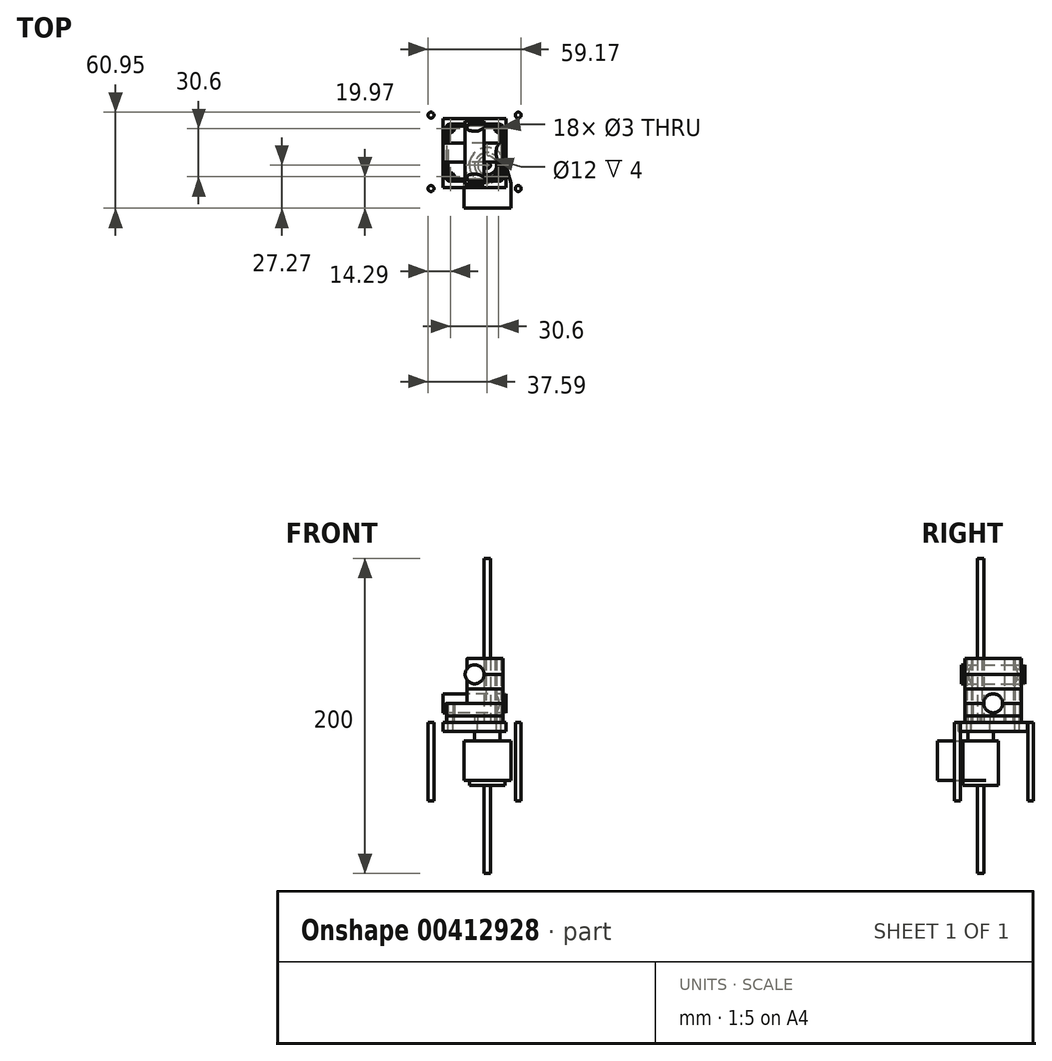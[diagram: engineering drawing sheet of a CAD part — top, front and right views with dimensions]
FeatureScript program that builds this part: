
annotation { "Feature Type Name" : "Feature", "Feature Type Description" : "" }
export const myFeature = defineFeature(function(context is Context, id is Id, definition is map)
    precondition{}
    {
        {
            var Q0;
            Q0=qCreatedBy(makeId("Top.planeOp"),FACE);
            cPlane(context, id + "F0", {"entities" : qUnion([Q0]), "cplaneType" : CPlaneType.OFFSET, "offset" : 3 * mm, "width" : 150 * mm, "height" : 150 * mm});
        }
        {
            var Q0;
            Q0=qCreatedBy(makeId("Top.planeOp"),FACE);
            cPlane(context, id + "F1", {"entities" : qUnion([Q0]), "cplaneType" : CPlaneType.OFFSET, "offset" : 1 * mm, "oppositeDirection" : true, "width" : 150 * mm, "height" : 150 * mm});
        }
        {
            var Q0;
            Q0=qCreatedBy(makeId("Right.planeOp"),FACE);
            var sketch = newSketch(context, id + "F2", { "sketchPlane" : qUnion([Q0])});
            skLineSegment(sketch, "E0", {"start": v(0, 0) * mm, "end": v(0, 11) * mm, "construction": true});
            skCircle(sketch, "E1", {"center": v(0, 11) * mm, "radius": 6 * mm});
            skSolve(sketch);
        }
        {
            var Q0;
            Q0=qCreatedBy(makeId("Front.planeOp"),FACE);
            var sketch = newSketch(context, id + "F3", { "sketchPlane" : qUnion([Q0])});
            skLineSegment(sketch, "E2", {"start": v(0, 0) * mm, "end": v(0, 29.4) * mm, "construction": true});
            skCircle(sketch, "E3", {"center": v(0, 29.4) * mm, "radius": 6 * mm});
            skSolve(sketch);
        }
        {
            var Q0;
            Q0=makeQuery(id+"F2.imprint","IMPRINT",FACE,{"disambiguationData":[TD([[makeQuery(id+"F2.imprint","IMPRINT",EDGE,{"derivedFrom":sQuery(id+"F2.wireOp",EDGE,"E1")}),1.0]])]});
            extrude(context, id + "F4", {"entities" : qUnion([Q0]), "depth" : 20 * mm, "hasSecondDirection" : true, "secondDirectionOppositeDirection" : true, "secondDirectionDepth" : 20 * mm});
        }
        {
            var Q0;
            Q0 = qSketchRegion(id + "F3", true);
            extrude(context, id + "F5", {"entities" : qUnion([Q0]), "depth" : 20 * mm, "hasSecondDirection" : true, "secondDirectionOppositeDirection" : true, "secondDirectionDepth" : 20 * mm});
        }
        {
            var Q0;
            Q0=qCreatedBy(id+"F0.planeOp",FACE);
            var sketch = newSketch(context, id + "F6", { "sketchPlane" : qUnion([Q0])});
            skPoint(sketch, "E4.middle", {"position": v(0, 0) * mm});
            skArc(sketch, "E5", {"start": v(-18, -8) * mm, "mid": v(-13.55, 0) * mm, "end": v(-18, 8) * mm});
            skPoint(sketch, "E6", {"position": v(18, 0) * mm});
            skArc(sketch, "E7", {"start": v(18, 8) * mm, "mid": v(13.55, 0) * mm, "end": v(18, -8) * mm});
            skCircle(sketch, "E8", {"center": v(-15.3, -15.3) * mm, "radius": 1.5 * mm});
            skCircle(sketch, "E9", {"center": v(15.3, -15.3) * mm, "radius": 1.5 * mm});
            skCircle(sketch, "E10", {"center": v(15.3, 15.3) * mm, "radius": 1.5 * mm});
            skCircle(sketch, "E11", {"center": v(-15.3, 15.3) * mm, "radius": 1.5 * mm});
            skCircle(sketch, "E12", {"center": v(15.3, -15.3) * mm, "radius": 2.25 * mm});
            skCircle(sketch, "E13", {"center": v(-15.3, -15.3) * mm, "radius": 2.5 * mm});
            skCircle(sketch, "E14", {"center": v(-15.3, 15.3) * mm, "radius": 2.5 * mm});
            skCircle(sketch, "E15", {"center": v(15.3, 15.3) * mm, "radius": 2.5 * mm});
            skLineSegment(sketch, "E16.bottom", {"start": v(-40, 30) * mm, "end": v(45, 30) * mm});
            skLineSegment(sketch, "E16.top", {"start": v(-40, -30) * mm, "end": v(45, -30) * mm});
            skLineSegment(sketch, "E16.left", {"start": v(-40, 30) * mm, "end": v(-40, -30) * mm});
            skLineSegment(sketch, "E16.right", {"start": v(45, 30) * mm, "end": v(45, -30) * mm});
            skLineSegment(sketch, "E17.bottom", {"start": v(18, 18) * mm, "end": v(-18, 18) * mm});
            skLineSegment(sketch, "E17.top", {"start": v(18, -18) * mm, "end": v(-18, -18) * mm});
            skLineSegment(sketch, "E17.left", {"start": v(18, 18) * mm, "end": v(18, -18) * mm});
            skLineSegment(sketch, "E17.right", {"start": v(-18, 18) * mm, "end": v(-18, -18) * mm});
            skLineSegment(sketch, "E18.0", {"start": v(16.8, 16.8) * mm, "end": v(-16.8, 16.8) * mm});
            skLineSegment(sketch, "E18.1", {"start": v(16.8, 16.8) * mm, "end": v(16.8, -16.8) * mm});
            skLineSegment(sketch, "E18.2", {"start": v(16.8, -16.8) * mm, "end": v(-16.8, -16.8) * mm});
            skLineSegment(sketch, "E18.3", {"start": v(-16.8, 16.8) * mm, "end": v(-16.8, -16.8) * mm});
            skSolve(sketch);
        }
        {
            var Q0;
            {var subQ0=sQuery(id+"F6.wireOp",EDGE,"E5");Q0=makeQuery(id+"F6.imprint","IMPRINT",FACE,{"disambiguationData":[TD([[makeQuery(id+"F6.imprint","IMPRINT",EDGE,{"derivedFrom":subQ0}),1.0]])]});}
            var Q1;
            {var subQ0=sQuery(id+"F6.wireOp",EDGE,"E7");Q1=makeQuery(id+"F6.imprint","IMPRINT",FACE,{"disambiguationData":[TD([[makeQuery(id+"F6.imprint","IMPRINT",EDGE,{"derivedFrom":subQ0}),1.0]])]});}
            var Q2;
            Q2=makeQuery(id+"F6.imprint","IMPRINT",FACE,{"disambiguationData":[TD([[makeQuery(id+"F6.imprint","IMPRINT",EDGE,{"derivedFrom":sQuery(id+"F6.wireOp",EDGE,"E4.bottom")}),1.0]])]});
            var Q3;
            {var subQ3=sQuery(id+"F6.wireOp",EDGE,"E8");Q3=makeQuery(id+"F6.imprint","IMPRINT",FACE,{"disambiguationData":[TD([[makeQuery(id+"F6.imprint","IMPRINT",EDGE,{"derivedFrom":subQ3}),-1.0]])]});}
            var Q4;
            {var subQ1=sQuery(id+"F6.wireOp",EDGE,"4588470f-8c88-46ac-a9e8-f2cc96a3f2d9.6");var subQ4=sQuery(id+"F6.wireOp",EDGE,"4588470f-8c88-46ac-a9e8-f2cc96a3f2d9.5");var subQ5=makeQuery(id+"F6.imprint","INTERSECT",VERTEX,{"derivedFrom":[subQ4,subQ1]});Q4=makeQuery(id+"F6.imprint","IMPRINT",FACE,{"disambiguationData":[TD([[makeQuery(id+"F6.imprint","IMPRINT",EDGE,{"disambiguationData":[TD([[subQ5,1.0]])],"derivedFrom":subQ4}),-1.0]])]});}
            var Q5;
            {var subQ1=sQuery(id+"F6.wireOp",EDGE,"4588470f-8c88-46ac-a9e8-f2cc96a3f2d9.3");var subQ6=sQuery(id+"F6.wireOp",EDGE,"4588470f-8c88-46ac-a9e8-f2cc96a3f2d9.1");var subQ7=makeQuery(id+"F6.imprint","INTERSECT",VERTEX,{"derivedFrom":[subQ6,subQ1]});Q5=makeQuery(id+"F6.imprint","IMPRINT",FACE,{"disambiguationData":[TD([[makeQuery(id+"F6.imprint","IMPRINT",EDGE,{"disambiguationData":[TD([[subQ7,1.0]])],"derivedFrom":subQ6}),1.0]])]});}
            var Q6;
            {var subQ3=sQuery(id+"F6.wireOp",EDGE,"E9");Q6=makeQuery(id+"F6.imprint","IMPRINT",FACE,{"disambiguationData":[TD([[makeQuery(id+"F6.imprint","IMPRINT",EDGE,{"derivedFrom":subQ3}),-1.0]])]});}
            var Q7;
            {var subQ1=sQuery(id+"F6.wireOp",EDGE,"4588470f-8c88-46ac-a9e8-f2cc96a3f2d9.0");var subQ5=sQuery(id+"F6.wireOp",EDGE,"4588470f-8c88-46ac-a9e8-f2cc96a3f2d9.1");var subQ6=makeQuery(id+"F6.imprint","INTERSECT",VERTEX,{"derivedFrom":[subQ1,subQ5]});Q7=makeQuery(id+"F6.imprint","IMPRINT",FACE,{"disambiguationData":[TD([[makeQuery(id+"F6.imprint","IMPRINT",EDGE,{"disambiguationData":[TD([[subQ6,-1.0]])],"derivedFrom":subQ1}),-1.0]])]});}
            var Q8;
            {var subQ1=sQuery(id+"F6.wireOp",EDGE,"4588470f-8c88-46ac-a9e8-f2cc96a3f2d9.4");var subQ4=sQuery(id+"F6.wireOp",EDGE,"4588470f-8c88-46ac-a9e8-f2cc96a3f2d9.2");var subQ5=makeQuery(id+"F6.imprint","INTERSECT",VERTEX,{"derivedFrom":[subQ4,subQ1]});Q8=makeQuery(id+"F6.imprint","IMPRINT",FACE,{"disambiguationData":[TD([[makeQuery(id+"F6.imprint","IMPRINT",EDGE,{"disambiguationData":[TD([[subQ5,1.0]])],"derivedFrom":subQ4}),-1.0]])]});}
            var Q9;
            {var subQ17=sQuery(id+"F6.wireOp",EDGE,"E17.bottom");Q9=makeQuery(id+"F6.imprint","IMPRINT",FACE,{"disambiguationData":[TD([[makeQuery(id+"F6.imprint","IMPRINT",EDGE,{"derivedFrom":subQ17}),1.0]])]});}
            var Q10;
            {var subQ0=sQuery(id+"F6.wireOp",EDGE,"E18.3");var subQ1=sQuery(id+"F6.wireOp",EDGE,"E5");var subQ2=makeQuery(id+"F6.imprint","INTERSECT",VERTEX,{"disambiguationData":[OD(0.0)],"derivedFrom":[subQ1,subQ0]});Q10=makeQuery(id+"F6.imprint","IMPRINT",FACE,{"disambiguationData":[TD([[makeQuery(id+"F6.imprint","IMPRINT",EDGE,{"disambiguationData":[TD([[subQ2,-1.0]])],"derivedFrom":subQ1}),1.0]])]});}
            var Q11;
            {var subQ1=sQuery(id+"F6.wireOp",EDGE,"E18.0");var subQ5=sQuery(id+"F6.wireOp",EDGE,"E14");var subQ6=makeQuery(id+"F6.imprint","INTERSECT",VERTEX,{"derivedFrom":[subQ5,subQ1]});Q11=makeQuery(id+"F6.imprint","IMPRINT",FACE,{"disambiguationData":[TD([[makeQuery(id+"F6.imprint","IMPRINT",EDGE,{"disambiguationData":[TD([[subQ6,-1.0]])],"derivedFrom":subQ5}),1.0]])]});}
            var Q12;
            {var subQ0=sQuery(id+"F6.wireOp",EDGE,"E18.0");var subQ1=sQuery(id+"F6.wireOp",EDGE,"E11");var subQ2=makeQuery(id+"F6.imprint","INTERSECT",VERTEX,{"derivedFrom":[subQ1,subQ0]});Q12=makeQuery(id+"F6.imprint","IMPRINT",FACE,{"disambiguationData":[TD([[makeQuery(id+"F6.imprint","IMPRINT",EDGE,{"disambiguationData":[TD([[subQ2,1.0]])],"derivedFrom":subQ1}),-1.0]])]});}
            var Q13;
            {var subQ0=sQuery(id+"F6.wireOp",EDGE,"E18.0");var subQ1=sQuery(id+"F6.wireOp",EDGE,"E11");var subQ2=makeQuery(id+"F6.imprint","INTERSECT",VERTEX,{"derivedFrom":[subQ1,subQ0]});Q13=makeQuery(id+"F6.imprint","IMPRINT",FACE,{"disambiguationData":[TD([[makeQuery(id+"F6.imprint","IMPRINT",EDGE,{"disambiguationData":[TD([[subQ2,-1.0]])],"derivedFrom":subQ1}),-1.0]])]});}
            var Q14;
            {var subQ0=sQuery(id+"F6.wireOp",EDGE,"E18.0");var subQ1=sQuery(id+"F6.wireOp",EDGE,"E10");var subQ2=makeQuery(id+"F6.imprint","INTERSECT",VERTEX,{"derivedFrom":[subQ1,subQ0]});Q14=makeQuery(id+"F6.imprint","IMPRINT",FACE,{"disambiguationData":[TD([[makeQuery(id+"F6.imprint","IMPRINT",EDGE,{"disambiguationData":[TD([[subQ2,-1.0]])],"derivedFrom":subQ1}),-1.0]])]});}
            var Q15;
            {var subQ0=sQuery(id+"F6.wireOp",EDGE,"E18.0");var subQ3=sQuery(id+"F6.wireOp",EDGE,"E15");var subQ4=makeQuery(id+"F6.imprint","INTERSECT",VERTEX,{"derivedFrom":[subQ3,subQ0]});Q15=makeQuery(id+"F6.imprint","IMPRINT",FACE,{"disambiguationData":[TD([[makeQuery(id+"F6.imprint","IMPRINT",EDGE,{"disambiguationData":[TD([[subQ4,1.0]])],"derivedFrom":subQ3}),1.0]])]});}
            var Q16;
            {var subQ0=sQuery(id+"F6.wireOp",EDGE,"E18.0");var subQ1=sQuery(id+"F6.wireOp",EDGE,"E10");var subQ2=makeQuery(id+"F6.imprint","INTERSECT",VERTEX,{"derivedFrom":[subQ1,subQ0]});Q16=makeQuery(id+"F6.imprint","IMPRINT",FACE,{"disambiguationData":[TD([[makeQuery(id+"F6.imprint","IMPRINT",EDGE,{"disambiguationData":[TD([[subQ2,1.0]])],"derivedFrom":subQ1}),-1.0]])]});}
            var Q17;
            {var subQ0=sQuery(id+"F6.wireOp",EDGE,"E18.1");var subQ1=sQuery(id+"F6.wireOp",EDGE,"E7");var subQ2=makeQuery(id+"F6.imprint","INTERSECT",VERTEX,{"disambiguationData":[OD(0.0)],"derivedFrom":[subQ1,subQ0]});Q17=makeQuery(id+"F6.imprint","IMPRINT",FACE,{"disambiguationData":[TD([[makeQuery(id+"F6.imprint","IMPRINT",EDGE,{"disambiguationData":[TD([[subQ2,-1.0]])],"derivedFrom":subQ1}),1.0]])]});}
            var Q18;
            {var subQ10=sQuery(id+"F6.wireOp",EDGE,"E17.top");Q18=makeQuery(id+"F6.imprint","IMPRINT",FACE,{"disambiguationData":[TD([[makeQuery(id+"F6.imprint","IMPRINT",EDGE,{"derivedFrom":subQ10}),-1.0]])]});}
            var Q19;
            {var subQ0=sQuery(id+"F6.wireOp",EDGE,"E18.1");var subQ1=sQuery(id+"F6.wireOp",EDGE,"E9");var subQ2=makeQuery(id+"F6.imprint","INTERSECT",VERTEX,{"derivedFrom":[subQ1,subQ0]});Q19=makeQuery(id+"F6.imprint","IMPRINT",FACE,{"disambiguationData":[TD([[makeQuery(id+"F6.imprint","IMPRINT",EDGE,{"disambiguationData":[TD([[subQ2,-1.0]])],"derivedFrom":subQ1}),-1.0]])]});}
            var Q20;
            {var subQ1=sQuery(id+"F6.wireOp",EDGE,"E18.1");var subQ6=sQuery(id+"F6.wireOp",EDGE,"E12");var subQ7=makeQuery(id+"F6.imprint","INTERSECT",VERTEX,{"derivedFrom":[subQ6,subQ1]});Q20=makeQuery(id+"F6.imprint","IMPRINT",FACE,{"disambiguationData":[TD([[makeQuery(id+"F6.imprint","IMPRINT",EDGE,{"disambiguationData":[TD([[subQ7,1.0]])],"derivedFrom":subQ6}),1.0]])]});}
            var Q21;
            {var subQ0=sQuery(id+"F6.wireOp",EDGE,"E18.2");var subQ1=sQuery(id+"F6.wireOp",EDGE,"E8");var subQ2=makeQuery(id+"F6.imprint","INTERSECT",VERTEX,{"derivedFrom":[subQ1,subQ0]});Q21=makeQuery(id+"F6.imprint","IMPRINT",FACE,{"disambiguationData":[TD([[makeQuery(id+"F6.imprint","IMPRINT",EDGE,{"disambiguationData":[TD([[subQ2,-1.0]])],"derivedFrom":subQ1}),-1.0]])]});}
            var Q22;
            {var subQ1=sQuery(id+"F6.wireOp",EDGE,"E18.2");var subQ5=sQuery(id+"F6.wireOp",EDGE,"E13");var subQ6=makeQuery(id+"F6.imprint","INTERSECT",VERTEX,{"derivedFrom":[subQ5,subQ1]});Q22=makeQuery(id+"F6.imprint","IMPRINT",FACE,{"disambiguationData":[TD([[makeQuery(id+"F6.imprint","IMPRINT",EDGE,{"disambiguationData":[TD([[subQ6,1.0]])],"derivedFrom":subQ5}),1.0]])]});}
            extrude(context, id + "F7", {"entities" : qUnion([Q0, Q1, Q2, Q3, Q4, Q5, Q6, Q7, Q8, Q9, Q10, Q11, Q12, Q13, Q14, Q15, Q16, Q17, Q18, Q19, Q20, Q21, Q22]), "depth" : 8 * mm});
        }
        {
            var Q0;
            Q0=makeQuery(id+"F7.opExtrude","CAP_FACE",FACE,{"disambiguationData":[OSD([sQuery(id+"F6.wireOp",EDGE,"E4.bottom"),sQuery(id+"F6.wireOp",EDGE,"E4.top"),sQuery(id+"F6.wireOp",EDGE,"E4.left"),sQuery(id+"F6.wireOp",EDGE,"E4.right"),sQuery(id+"F6.wireOp",EDGE,"0e375415-61ae-43ef-ae01-274447b75c67.filletArc"),sQuery(id+"F6.wireOp",EDGE,"dcf4f1b7-a445-47e3-85c1-2e5db65cd479.filletArc"),sQuery(id+"F6.wireOp",EDGE,"fe098dff-6007-4556-b7ac-c9266c39542a.filletArc"),sQuery(id+"F6.wireOp",EDGE,"ced4e515-334f-42f5-9fe0-b6419f4f79bf.filletArc"),sQuery(id+"F6.wireOp",EDGE,"4588470f-8c88-46ac-a9e8-f2cc96a3f2d9.0"),sQuery(id+"F6.wireOp",EDGE,"4588470f-8c88-46ac-a9e8-f2cc96a3f2d9.1"),sQuery(id+"F6.wireOp",EDGE,"4588470f-8c88-46ac-a9e8-f2cc96a3f2d9.2"),sQuery(id+"F6.wireOp",EDGE,"4588470f-8c88-46ac-a9e8-f2cc96a3f2d9.3"),sQuery(id+"F6.wireOp",EDGE,"4588470f-8c88-46ac-a9e8-f2cc96a3f2d9.4"),sQuery(id+"F6.wireOp",EDGE,"4588470f-8c88-46ac-a9e8-f2cc96a3f2d9.5"),sQuery(id+"F6.wireOp",EDGE,"4588470f-8c88-46ac-a9e8-f2cc96a3f2d9.6"),sQuery(id+"F6.wireOp",EDGE,"4588470f-8c88-46ac-a9e8-f2cc96a3f2d9.7"),sQuery(id+"F6.wireOp",EDGE,"E5"),sQuery(id+"F6.wireOp",EDGE,"E7")])],"isStart":false});
            var sketch = newSketch(context, id + "F8", { "sketchPlane" : qUnion([Q0])});
            skArc(sketch, "E19", {"start": v(-8, 18) * mm, "mid": v(0, 13.55) * mm, "end": v(8, 18) * mm});
            skArc(sketch, "E20", {"start": v(8, -18) * mm, "mid": v(0, -13.55) * mm, "end": v(-8, -18) * mm});
            skSolve(sketch);
        }
        {
            var Q0;
            Q0=makeQuery(id+"F8.imprint","IMPRINT",FACE,{"disambiguationData":[TD([[makeQuery(id+"F8.imprint","IMPRINT",EDGE,{"derivedFrom":makeQuery(id+"F7.opExtrude","CAP_EDGE",EDGE,{"disambiguationData":[OSD([sQuery(id+"F6.wireOp",EDGE,"E4.bottom")])],"isStart":false})}),1.0]])]});
            var Q1;
            {var subQ0=sQuery(id+"F8.wireOp",EDGE,"E19");Q1=makeQuery(id+"F8.imprint","IMPRINT",FACE,{"disambiguationData":[TD([[makeQuery(id+"F8.imprint","IMPRINT",EDGE,{"derivedFrom":subQ0}),1.0]])]});}
            var Q2;
            {var subQ0=sQuery(id+"F8.wireOp",EDGE,"AOsfK3JN-hG8h-P0De-w1nV-t2gnGfcndvQp");var subQ1=makeQuery(id+"F7.opExtrude","CAP_EDGE",EDGE,{"disambiguationData":[OSD([sQuery(id+"F6.wireOp",EDGE,"4588470f-8c88-46ac-a9e8-f2cc96a3f2d9.7")])],"isStart":false});var subQ2=makeQuery(id+"F8.imprint","INTERSECT",VERTEX,{"disambiguationData":[OD(0.0)],"derivedFrom":[subQ1,subQ0]});Q2=makeQuery(id+"F8.imprint","IMPRINT",FACE,{"disambiguationData":[TD([[makeQuery(id+"F8.imprint","IMPRINT",EDGE,{"disambiguationData":[TD([[subQ2,-1.0]])],"derivedFrom":subQ0}),1.0]])]});}
            var Q3;
            {var subQ0=sQuery(id+"F8.wireOp",EDGE,"E20");Q3=makeQuery(id+"F8.imprint","IMPRINT",FACE,{"disambiguationData":[TD([[makeQuery(id+"F8.imprint","IMPRINT",EDGE,{"derivedFrom":subQ0}),1.0]])]});}
            var Q4;
            {var subQ0=sQuery(id+"F8.wireOp",EDGE,"E19");var subQ1=makeQuery(id+"F7.opExtrude","CAP_EDGE",EDGE,{"disambiguationData":[OSD([sQuery(id+"F6.wireOp",EDGE,"E18.0")])],"isStart":false});var subQ2=makeQuery(id+"F8.imprint","INTERSECT",VERTEX,{"disambiguationData":[OD(0.0)],"derivedFrom":[subQ1,subQ0]});Q4=makeQuery(id+"F8.imprint","IMPRINT",FACE,{"disambiguationData":[TD([[makeQuery(id+"F8.imprint","IMPRINT",EDGE,{"disambiguationData":[TD([[subQ2,-1.0]])],"derivedFrom":subQ0}),1.0]])]});}
            var Q5;
            {var subQ0=sQuery(id+"F8.wireOp",EDGE,"E20");var subQ1=makeQuery(id+"F7.opExtrude","CAP_EDGE",EDGE,{"disambiguationData":[OSD([sQuery(id+"F6.wireOp",EDGE,"E18.2")])],"isStart":false});var subQ2=makeQuery(id+"F8.imprint","INTERSECT",VERTEX,{"disambiguationData":[OD(0.0)],"derivedFrom":[subQ1,subQ0]});Q5=makeQuery(id+"F8.imprint","IMPRINT",FACE,{"disambiguationData":[TD([[makeQuery(id+"F8.imprint","IMPRINT",EDGE,{"disambiguationData":[TD([[subQ2,-1.0]])],"derivedFrom":subQ0}),1.0]])]});}
            var Q6;
            {var subQ1=sQuery(id+"F6.wireOp",EDGE,"E5");Q6=makeQuery(id+"F8.imprint","IMPRINT",FACE,{"disambiguationData":[TD([[makeQuery(id+"F8.imprint","IMPRINT",EDGE,{"derivedFrom":makeQuery(id+"F7.opExtrude","CAP_EDGE",EDGE,{"disambiguationData":[OSD([subQ1])],"isStart":false})}),1.0]])]});}
            var Q7;
            {var subQ1=sQuery(id+"F6.wireOp",EDGE,"E7");Q7=makeQuery(id+"F8.imprint","IMPRINT",FACE,{"disambiguationData":[TD([[makeQuery(id+"F8.imprint","IMPRINT",EDGE,{"derivedFrom":makeQuery(id+"F7.opExtrude","CAP_EDGE",EDGE,{"disambiguationData":[OSD([subQ1])],"isStart":false})}),1.0]])]});}
            extrude(context, id + "F9", {"entities" : qUnion([Q0, Q1, Q2, Q3, Q4, Q5, Q6, Q7]), "depth" : 9.2 * mm});
        }
        {
            var Q0;
            Q0=makeQuery(id+"F9.opExtrude","CAP_FACE",FACE,{"disambiguationData":[OSD([sQuery(id+"F6.wireOp",EDGE,"E4.bottom"),sQuery(id+"F6.wireOp",EDGE,"E4.top"),sQuery(id+"F6.wireOp",EDGE,"E4.left"),sQuery(id+"F6.wireOp",EDGE,"E4.right"),sQuery(id+"F6.wireOp",EDGE,"0e375415-61ae-43ef-ae01-274447b75c67.filletArc"),sQuery(id+"F6.wireOp",EDGE,"dcf4f1b7-a445-47e3-85c1-2e5db65cd479.filletArc"),sQuery(id+"F6.wireOp",EDGE,"fe098dff-6007-4556-b7ac-c9266c39542a.filletArc"),sQuery(id+"F6.wireOp",EDGE,"ced4e515-334f-42f5-9fe0-b6419f4f79bf.filletArc"),sQuery(id+"F6.wireOp",EDGE,"4588470f-8c88-46ac-a9e8-f2cc96a3f2d9.1"),sQuery(id+"F6.wireOp",EDGE,"4588470f-8c88-46ac-a9e8-f2cc96a3f2d9.2"),sQuery(id+"F6.wireOp",EDGE,"4588470f-8c88-46ac-a9e8-f2cc96a3f2d9.5"),sQuery(id+"F6.wireOp",EDGE,"4588470f-8c88-46ac-a9e8-f2cc96a3f2d9.7"),sQuery(id+"F6.wireOp",EDGE,"E5"),sQuery(id+"F6.wireOp",EDGE,"E7"),sQuery(id+"F6.wireOp",EDGE,"E8"),sQuery(id+"F6.wireOp",EDGE,"E9"),sQuery(id+"F6.wireOp",EDGE,"E10"),sQuery(id+"F6.wireOp",EDGE,"E11"),sQuery(id+"F6.wireOp",EDGE,"E12"),sQuery(id+"F6.wireOp",EDGE,"E13"),sQuery(id+"F6.wireOp",EDGE,"E14"),sQuery(id+"F6.wireOp",EDGE,"E15"),sQuery(id+"F8.wireOp",EDGE,"E19"),sQuery(id+"F8.wireOp",EDGE,"E20")])],"isStart":false});
            extrude(context, id + "F10", {"entities" : qUnion([Q0]), "depth" : 9.2 * mm});
        }
        {
            var Q0;
            Q0=makeQuery(id+"F10.opExtrude","CAP_FACE",FACE,{"disambiguationData":[OSD([sQuery(id+"F6.wireOp",EDGE,"E4.bottom"),sQuery(id+"F6.wireOp",EDGE,"E4.top"),sQuery(id+"F6.wireOp",EDGE,"E4.left"),sQuery(id+"F6.wireOp",EDGE,"E4.right"),sQuery(id+"F6.wireOp",EDGE,"0e375415-61ae-43ef-ae01-274447b75c67.filletArc"),sQuery(id+"F6.wireOp",EDGE,"dcf4f1b7-a445-47e3-85c1-2e5db65cd479.filletArc"),sQuery(id+"F6.wireOp",EDGE,"fe098dff-6007-4556-b7ac-c9266c39542a.filletArc"),sQuery(id+"F6.wireOp",EDGE,"ced4e515-334f-42f5-9fe0-b6419f4f79bf.filletArc"),sQuery(id+"F6.wireOp",EDGE,"4588470f-8c88-46ac-a9e8-f2cc96a3f2d9.1"),sQuery(id+"F6.wireOp",EDGE,"4588470f-8c88-46ac-a9e8-f2cc96a3f2d9.2"),sQuery(id+"F6.wireOp",EDGE,"4588470f-8c88-46ac-a9e8-f2cc96a3f2d9.5"),sQuery(id+"F6.wireOp",EDGE,"4588470f-8c88-46ac-a9e8-f2cc96a3f2d9.7"),sQuery(id+"F6.wireOp",EDGE,"E5"),sQuery(id+"F6.wireOp",EDGE,"E7"),sQuery(id+"F6.wireOp",EDGE,"E8"),sQuery(id+"F6.wireOp",EDGE,"E9"),sQuery(id+"F6.wireOp",EDGE,"E10"),sQuery(id+"F6.wireOp",EDGE,"E11"),sQuery(id+"F6.wireOp",EDGE,"E12"),sQuery(id+"F6.wireOp",EDGE,"E13"),sQuery(id+"F6.wireOp",EDGE,"E14"),sQuery(id+"F6.wireOp",EDGE,"E15"),sQuery(id+"F8.wireOp",EDGE,"E19"),sQuery(id+"F8.wireOp",EDGE,"E20")])],"isStart":false});
            var sketch = newSketch(context, id + "F11", { "sketchPlane" : qUnion([Q0])});
            skLineSegment(sketch, "E21", {"start": v(-16.8, -7.12) * mm, "end": v(-16.8, -7.12) * mm});
            skLineSegment(sketch, "E22", {"start": v(16.8, 7.12) * mm, "end": v(16.8, 7.12) * mm});
            skSolve(sketch);
        }
        {
            var Q0;
            Q0=makeQuery(id+"F11.imprint","IMPRINT",FACE,{"disambiguationData":[TD([[makeQuery(id+"F11.imprint","IMPRINT",EDGE,{"derivedFrom":sQuery(id+"F11.wireOp",EDGE,"E21")}),-1.0]])]});
            var Q1;
            {var subQ3=sQuery(id+"F8.wireOp",EDGE,"E19");Q1=makeQuery(id+"F11.imprint","IMPRINT",FACE,{"disambiguationData":[TD([[makeQuery(id+"F11.imprint","IMPRINT",EDGE,{"derivedFrom":makeQuery(id+"F10.opExtrude","CAP_EDGE",EDGE,{"disambiguationData":[OSD([subQ3])],"isStart":false})}),1.0]])]});}
            extrude(context, id + "F12", {"entities" : qUnion([Q0, Q1]), "depth" : 10 * mm});
        }
        {
            var Q0;
            Q0=makeQuery(id+"F5.opExtrude","SWEPT_BODY",BODY,{"disambiguationData":[OSD([sQuery(id+"F3.wireOp",EDGE,"E3")])]});
            var Q1;
            Q1=makeQuery(id+"F4.opExtrude","SWEPT_BODY",BODY,{"disambiguationData":[OSD([sQuery(id+"F2.wireOp",EDGE,"E1")])]});
            var Q2;
            Q2=makeQuery(id+"F9.opExtrude","SWEPT_BODY",BODY,{"disambiguationData":[OSD([sQuery(id+"F6.wireOp",EDGE,"E4.bottom"),sQuery(id+"F6.wireOp",EDGE,"E4.top"),sQuery(id+"F6.wireOp",EDGE,"E4.left"),sQuery(id+"F6.wireOp",EDGE,"E4.right"),sQuery(id+"F6.wireOp",EDGE,"0e375415-61ae-43ef-ae01-274447b75c67.filletArc"),sQuery(id+"F6.wireOp",EDGE,"dcf4f1b7-a445-47e3-85c1-2e5db65cd479.filletArc"),sQuery(id+"F6.wireOp",EDGE,"fe098dff-6007-4556-b7ac-c9266c39542a.filletArc"),sQuery(id+"F6.wireOp",EDGE,"ced4e515-334f-42f5-9fe0-b6419f4f79bf.filletArc"),sQuery(id+"F6.wireOp",EDGE,"4588470f-8c88-46ac-a9e8-f2cc96a3f2d9.1"),sQuery(id+"F6.wireOp",EDGE,"4588470f-8c88-46ac-a9e8-f2cc96a3f2d9.2"),sQuery(id+"F6.wireOp",EDGE,"4588470f-8c88-46ac-a9e8-f2cc96a3f2d9.5"),sQuery(id+"F6.wireOp",EDGE,"4588470f-8c88-46ac-a9e8-f2cc96a3f2d9.7"),sQuery(id+"F6.wireOp",EDGE,"E5"),sQuery(id+"F6.wireOp",EDGE,"E7"),sQuery(id+"F6.wireOp",EDGE,"E8"),sQuery(id+"F6.wireOp",EDGE,"E9"),sQuery(id+"F6.wireOp",EDGE,"E10"),sQuery(id+"F6.wireOp",EDGE,"E11"),sQuery(id+"F6.wireOp",EDGE,"E12"),sQuery(id+"F6.wireOp",EDGE,"E13"),sQuery(id+"F6.wireOp",EDGE,"E14"),sQuery(id+"F6.wireOp",EDGE,"E15"),sQuery(id+"F8.wireOp",EDGE,"E19"),sQuery(id+"F8.wireOp",EDGE,"E20")])]});
            var Q3;
            Q3=makeQuery(id+"F10.opExtrude","SWEPT_BODY",BODY,{"disambiguationData":[OSD([sQuery(id+"F6.wireOp",EDGE,"E4.bottom"),sQuery(id+"F6.wireOp",EDGE,"E4.top"),sQuery(id+"F6.wireOp",EDGE,"E4.left"),sQuery(id+"F6.wireOp",EDGE,"E4.right"),sQuery(id+"F6.wireOp",EDGE,"0e375415-61ae-43ef-ae01-274447b75c67.filletArc"),sQuery(id+"F6.wireOp",EDGE,"dcf4f1b7-a445-47e3-85c1-2e5db65cd479.filletArc"),sQuery(id+"F6.wireOp",EDGE,"fe098dff-6007-4556-b7ac-c9266c39542a.filletArc"),sQuery(id+"F6.wireOp",EDGE,"ced4e515-334f-42f5-9fe0-b6419f4f79bf.filletArc"),sQuery(id+"F6.wireOp",EDGE,"4588470f-8c88-46ac-a9e8-f2cc96a3f2d9.1"),sQuery(id+"F6.wireOp",EDGE,"4588470f-8c88-46ac-a9e8-f2cc96a3f2d9.2"),sQuery(id+"F6.wireOp",EDGE,"4588470f-8c88-46ac-a9e8-f2cc96a3f2d9.5"),sQuery(id+"F6.wireOp",EDGE,"4588470f-8c88-46ac-a9e8-f2cc96a3f2d9.7"),sQuery(id+"F6.wireOp",EDGE,"E5"),sQuery(id+"F6.wireOp",EDGE,"E7"),sQuery(id+"F6.wireOp",EDGE,"E8"),sQuery(id+"F6.wireOp",EDGE,"E9"),sQuery(id+"F6.wireOp",EDGE,"E10"),sQuery(id+"F6.wireOp",EDGE,"E11"),sQuery(id+"F6.wireOp",EDGE,"E12"),sQuery(id+"F6.wireOp",EDGE,"E13"),sQuery(id+"F6.wireOp",EDGE,"E14"),sQuery(id+"F6.wireOp",EDGE,"E15"),sQuery(id+"F8.wireOp",EDGE,"E19"),sQuery(id+"F8.wireOp",EDGE,"E20")])]});
            var Q4;
            Q4=makeQuery(id+"F12.opExtrude","SWEPT_BODY",BODY,{"disambiguationData":[OSD([sQuery(id+"F6.wireOp",EDGE,"E4.bottom"),sQuery(id+"F6.wireOp",EDGE,"E4.top"),sQuery(id+"F6.wireOp",EDGE,"E4.left"),sQuery(id+"F6.wireOp",EDGE,"E4.right"),sQuery(id+"F6.wireOp",EDGE,"0e375415-61ae-43ef-ae01-274447b75c67.filletArc"),sQuery(id+"F6.wireOp",EDGE,"dcf4f1b7-a445-47e3-85c1-2e5db65cd479.filletArc"),sQuery(id+"F6.wireOp",EDGE,"fe098dff-6007-4556-b7ac-c9266c39542a.filletArc"),sQuery(id+"F6.wireOp",EDGE,"ced4e515-334f-42f5-9fe0-b6419f4f79bf.filletArc"),sQuery(id+"F6.wireOp",EDGE,"4588470f-8c88-46ac-a9e8-f2cc96a3f2d9.1"),sQuery(id+"F6.wireOp",EDGE,"4588470f-8c88-46ac-a9e8-f2cc96a3f2d9.2"),sQuery(id+"F6.wireOp",EDGE,"4588470f-8c88-46ac-a9e8-f2cc96a3f2d9.5"),sQuery(id+"F6.wireOp",EDGE,"4588470f-8c88-46ac-a9e8-f2cc96a3f2d9.7"),sQuery(id+"F6.wireOp",EDGE,"E8"),sQuery(id+"F6.wireOp",EDGE,"E9"),sQuery(id+"F6.wireOp",EDGE,"E10"),sQuery(id+"F6.wireOp",EDGE,"E11"),sQuery(id+"F6.wireOp",EDGE,"E12"),sQuery(id+"F6.wireOp",EDGE,"E13"),sQuery(id+"F6.wireOp",EDGE,"E14"),sQuery(id+"F6.wireOp",EDGE,"E15"),sQuery(id+"F8.wireOp",EDGE,"E19"),sQuery(id+"F8.wireOp",EDGE,"E20"),sQuery(id+"F11.wireOp",EDGE,"E21"),sQuery(id+"F11.wireOp",EDGE,"E22")])]});
            var Q5;
            Q5=makeQuery(id+"F7.opExtrude","SWEPT_BODY",BODY,{"disambiguationData":[OSD([sQuery(id+"F6.wireOp",EDGE,"E4.bottom"),sQuery(id+"F6.wireOp",EDGE,"E4.top"),sQuery(id+"F6.wireOp",EDGE,"E4.left"),sQuery(id+"F6.wireOp",EDGE,"E4.right"),sQuery(id+"F6.wireOp",EDGE,"0e375415-61ae-43ef-ae01-274447b75c67.filletArc"),sQuery(id+"F6.wireOp",EDGE,"dcf4f1b7-a445-47e3-85c1-2e5db65cd479.filletArc"),sQuery(id+"F6.wireOp",EDGE,"fe098dff-6007-4556-b7ac-c9266c39542a.filletArc"),sQuery(id+"F6.wireOp",EDGE,"ced4e515-334f-42f5-9fe0-b6419f4f79bf.filletArc"),sQuery(id+"F6.wireOp",EDGE,"4588470f-8c88-46ac-a9e8-f2cc96a3f2d9.1"),sQuery(id+"F6.wireOp",EDGE,"4588470f-8c88-46ac-a9e8-f2cc96a3f2d9.2"),sQuery(id+"F6.wireOp",EDGE,"4588470f-8c88-46ac-a9e8-f2cc96a3f2d9.5"),sQuery(id+"F6.wireOp",EDGE,"4588470f-8c88-46ac-a9e8-f2cc96a3f2d9.7"),sQuery(id+"F6.wireOp",EDGE,"E5"),sQuery(id+"F6.wireOp",EDGE,"E7"),sQuery(id+"F6.wireOp",EDGE,"E8"),sQuery(id+"F6.wireOp",EDGE,"E9"),sQuery(id+"F6.wireOp",EDGE,"E10"),sQuery(id+"F6.wireOp",EDGE,"E11"),sQuery(id+"F6.wireOp",EDGE,"E12"),sQuery(id+"F6.wireOp",EDGE,"E13"),sQuery(id+"F6.wireOp",EDGE,"E14"),sQuery(id+"F6.wireOp",EDGE,"E15")])]});
            booleanBodies(context, id + "F13", {"operationType" : BooleanOperationType.SUBTRACTION, "tools" : qUnion([Q0, Q1]), "targets" : qUnion([Q2, Q3, Q4, Q5]), "keepTools" : true});
        }
        {
            var Q0;
            Q0=qCreatedBy(id+"F0.planeOp",FACE);
            var sketch = newSketch(context, id + "F14", { "sketchPlane" : qUnion([Q0])});
            skCircle(sketch, "E23", {"center": v(8, -8) * mm, "radius": 2 * mm});
            skSolve(sketch);
        }
        {
            var Q0;
            Q0=makeQuery(id+"F14.imprint","IMPRINT",FACE,{"disambiguationData":[TD([[makeQuery(id+"F14.imprint","IMPRINT",EDGE,{"derivedFrom":sQuery(id+"F14.wireOp",EDGE,"E23")}),1.0]])]});
            extrude(context, id + "F15", {"entities" : qUnion([Q0]), "depth" : 100 * mm, "hasSecondDirection" : true, "secondDirectionOppositeDirection" : true, "secondDirectionDepth" : 100 * mm});
        }
        {
            var Q0;
            Q0=qCreatedBy(id+"F1.planeOp",FACE);
            var sketch = newSketch(context, id + "F16", { "sketchPlane" : qUnion([Q0])});
            skCircle(sketch, "E24", {"center": v(8, -8) * mm, "radius": 6 * mm});
            skCircle(sketch, "E25", {"center": v(8, -8) * mm, "radius": 8 * mm});
            skSolve(sketch);
        }
        {
            var Q0;
            Q0=makeQuery(id+"F16.imprint","IMPRINT",FACE,{"disambiguationData":[TD([[makeQuery(id+"F16.imprint","IMPRINT",EDGE,{"derivedFrom":sQuery(id+"F16.wireOp",EDGE,"E24")}),-1.0]])]});
            extrude(context, id + "F17", {"entities" : qUnion([Q0]), "depth" : 4 * mm});
        }
        {
            var Q0;
            Q0=makeQuery(id+"F16.imprint","IMPRINT",FACE,{"disambiguationData":[TD([[makeQuery(id+"F16.imprint","IMPRINT",EDGE,{"derivedFrom":sQuery(id+"F16.wireOp",EDGE,"E24")}),1.0]])]});
            extrude(context, id + "F18", {"entities" : qUnion([Q0]), "operationType" : NewBodyOperationType.ADD, "oppositeDirection" : true, "depth" : 6 * mm});
        }
        {
            var Q0;
            Q0=makeQuery(id+"F18.opExtrude","CAP_FACE",FACE,{"disambiguationData":[OSD([sQuery(id+"F16.wireOp",EDGE,"E24")])],"isStart":false});
            var sketch = newSketch(context, id + "F19", { "sketchPlane" : qUnion([Q0])});
            skCircle(sketch, "E26", {"center": v(8, 8) * mm, "radius": 8 * mm});
            skSolve(sketch);
        }
        {
            var Q0;
            {var subQ17=sQuery(id+"F6.wireOp",EDGE,"E17.bottom");Q0=makeQuery(id+"F6.imprint","IMPRINT",FACE,{"disambiguationData":[TD([[makeQuery(id+"F6.imprint","IMPRINT",EDGE,{"derivedFrom":subQ17}),1.0]])]});}
            var Q1;
            {var subQ0=sQuery(id+"F6.wireOp",EDGE,"E18.0");var subQ3=sQuery(id+"F6.wireOp",EDGE,"E15");var subQ4=makeQuery(id+"F6.imprint","INTERSECT",VERTEX,{"derivedFrom":[subQ3,subQ0]});Q1=makeQuery(id+"F6.imprint","IMPRINT",FACE,{"disambiguationData":[TD([[makeQuery(id+"F6.imprint","IMPRINT",EDGE,{"disambiguationData":[TD([[subQ4,1.0]])],"derivedFrom":subQ3}),1.0]])]});}
            var Q2;
            {var subQ0=sQuery(id+"F6.wireOp",EDGE,"E18.0");var subQ1=sQuery(id+"F6.wireOp",EDGE,"E10");var subQ2=makeQuery(id+"F6.imprint","INTERSECT",VERTEX,{"derivedFrom":[subQ1,subQ0]});Q2=makeQuery(id+"F6.imprint","IMPRINT",FACE,{"disambiguationData":[TD([[makeQuery(id+"F6.imprint","IMPRINT",EDGE,{"disambiguationData":[TD([[subQ2,1.0]])],"derivedFrom":subQ1}),-1.0]])]});}
            var Q3;
            {var subQ0=sQuery(id+"F6.wireOp",EDGE,"E18.0");var subQ1=sQuery(id+"F6.wireOp",EDGE,"E10");var subQ2=makeQuery(id+"F6.imprint","INTERSECT",VERTEX,{"derivedFrom":[subQ1,subQ0]});Q3=makeQuery(id+"F6.imprint","IMPRINT",FACE,{"disambiguationData":[TD([[makeQuery(id+"F6.imprint","IMPRINT",EDGE,{"disambiguationData":[TD([[subQ2,-1.0]])],"derivedFrom":subQ1}),-1.0]])]});}
            var Q4;
            {var subQ1=sQuery(id+"F6.wireOp",EDGE,"E18.0");var subQ5=sQuery(id+"F6.wireOp",EDGE,"E14");var subQ6=makeQuery(id+"F6.imprint","INTERSECT",VERTEX,{"derivedFrom":[subQ5,subQ1]});Q4=makeQuery(id+"F6.imprint","IMPRINT",FACE,{"disambiguationData":[TD([[makeQuery(id+"F6.imprint","IMPRINT",EDGE,{"disambiguationData":[TD([[subQ6,-1.0]])],"derivedFrom":subQ5}),1.0]])]});}
            var Q5;
            {var subQ0=sQuery(id+"F6.wireOp",EDGE,"E18.0");var subQ1=sQuery(id+"F6.wireOp",EDGE,"E11");var subQ2=makeQuery(id+"F6.imprint","INTERSECT",VERTEX,{"derivedFrom":[subQ1,subQ0]});Q5=makeQuery(id+"F6.imprint","IMPRINT",FACE,{"disambiguationData":[TD([[makeQuery(id+"F6.imprint","IMPRINT",EDGE,{"disambiguationData":[TD([[subQ2,-1.0]])],"derivedFrom":subQ1}),-1.0]])]});}
            var Q6;
            {var subQ0=sQuery(id+"F6.wireOp",EDGE,"E18.0");var subQ1=sQuery(id+"F6.wireOp",EDGE,"E11");var subQ2=makeQuery(id+"F6.imprint","INTERSECT",VERTEX,{"derivedFrom":[subQ1,subQ0]});Q6=makeQuery(id+"F6.imprint","IMPRINT",FACE,{"disambiguationData":[TD([[makeQuery(id+"F6.imprint","IMPRINT",EDGE,{"disambiguationData":[TD([[subQ2,1.0]])],"derivedFrom":subQ1}),-1.0]])]});}
            var Q7;
            {var subQ0=sQuery(id+"F6.wireOp",EDGE,"E17.right");var subQ1=sQuery(id+"F6.wireOp",EDGE,"E5");var subQ2=makeQuery(id+"F6.imprint","INTERSECT",VERTEX,{"disambiguationData":[OD(0.0)],"derivedFrom":[subQ1,subQ0]});Q7=makeQuery(id+"F6.imprint","IMPRINT",FACE,{"disambiguationData":[TD([[makeQuery(id+"F6.imprint","IMPRINT",EDGE,{"disambiguationData":[TD([[subQ2,-1.0]])],"derivedFrom":subQ1}),1.0]])]});}
            var Q8;
            {var subQ0=sQuery(id+"F6.wireOp",EDGE,"E18.2");var subQ1=sQuery(id+"F6.wireOp",EDGE,"E8");var subQ2=makeQuery(id+"F6.imprint","INTERSECT",VERTEX,{"derivedFrom":[subQ1,subQ0]});Q8=makeQuery(id+"F6.imprint","IMPRINT",FACE,{"disambiguationData":[TD([[makeQuery(id+"F6.imprint","IMPRINT",EDGE,{"disambiguationData":[TD([[subQ2,-1.0]])],"derivedFrom":subQ1}),-1.0]])]});}
            var Q9;
            {var subQ0=sQuery(id+"F6.wireOp",EDGE,"E18.2");var subQ1=sQuery(id+"F6.wireOp",EDGE,"E8");var subQ2=makeQuery(id+"F6.imprint","INTERSECT",VERTEX,{"derivedFrom":[subQ1,subQ0]});Q9=makeQuery(id+"F6.imprint","IMPRINT",FACE,{"disambiguationData":[TD([[makeQuery(id+"F6.imprint","IMPRINT",EDGE,{"disambiguationData":[TD([[subQ2,1.0]])],"derivedFrom":subQ1}),-1.0]])]});}
            var Q10;
            {var subQ10=sQuery(id+"F6.wireOp",EDGE,"E17.top");Q10=makeQuery(id+"F6.imprint","IMPRINT",FACE,{"disambiguationData":[TD([[makeQuery(id+"F6.imprint","IMPRINT",EDGE,{"derivedFrom":subQ10}),-1.0]])]});}
            var Q11;
            {var subQ1=sQuery(id+"F6.wireOp",EDGE,"E18.2");var subQ5=sQuery(id+"F6.wireOp",EDGE,"E13");var subQ6=makeQuery(id+"F6.imprint","INTERSECT",VERTEX,{"derivedFrom":[subQ5,subQ1]});Q11=makeQuery(id+"F6.imprint","IMPRINT",FACE,{"disambiguationData":[TD([[makeQuery(id+"F6.imprint","IMPRINT",EDGE,{"disambiguationData":[TD([[subQ6,1.0]])],"derivedFrom":subQ5}),1.0]])]});}
            var Q12;
            {var subQ0=sQuery(id+"F6.wireOp",EDGE,"E18.1");var subQ1=sQuery(id+"F6.wireOp",EDGE,"E9");var subQ2=makeQuery(id+"F6.imprint","INTERSECT",VERTEX,{"derivedFrom":[subQ1,subQ0]});Q12=makeQuery(id+"F6.imprint","IMPRINT",FACE,{"disambiguationData":[TD([[makeQuery(id+"F6.imprint","IMPRINT",EDGE,{"disambiguationData":[TD([[subQ2,1.0]])],"derivedFrom":subQ1}),-1.0]])]});}
            var Q13;
            {var subQ1=sQuery(id+"F6.wireOp",EDGE,"E18.1");var subQ6=sQuery(id+"F6.wireOp",EDGE,"E12");var subQ7=makeQuery(id+"F6.imprint","INTERSECT",VERTEX,{"derivedFrom":[subQ6,subQ1]});Q13=makeQuery(id+"F6.imprint","IMPRINT",FACE,{"disambiguationData":[TD([[makeQuery(id+"F6.imprint","IMPRINT",EDGE,{"disambiguationData":[TD([[subQ7,1.0]])],"derivedFrom":subQ6}),1.0]])]});}
            var Q14;
            {var subQ0=sQuery(id+"F6.wireOp",EDGE,"E18.1");var subQ1=sQuery(id+"F6.wireOp",EDGE,"E9");var subQ2=makeQuery(id+"F6.imprint","INTERSECT",VERTEX,{"derivedFrom":[subQ1,subQ0]});Q14=makeQuery(id+"F6.imprint","IMPRINT",FACE,{"disambiguationData":[TD([[makeQuery(id+"F6.imprint","IMPRINT",EDGE,{"disambiguationData":[TD([[subQ2,-1.0]])],"derivedFrom":subQ1}),-1.0]])]});}
            var Q15;
            {var subQ0=sQuery(id+"F6.wireOp",EDGE,"E17.left");var subQ1=sQuery(id+"F6.wireOp",EDGE,"E7");var subQ2=makeQuery(id+"F6.imprint","INTERSECT",VERTEX,{"disambiguationData":[OD(0.0)],"derivedFrom":[subQ1,subQ0]});Q15=makeQuery(id+"F6.imprint","IMPRINT",FACE,{"disambiguationData":[TD([[makeQuery(id+"F6.imprint","IMPRINT",EDGE,{"disambiguationData":[TD([[subQ2,-1.0]])],"derivedFrom":subQ1}),1.0]])]});}
            extrude(context, id + "F20", {"entities" : qUnion([Q0, Q1, Q2, Q3, Q4, Q5, Q6, Q7, Q8, Q9, Q10, Q11, Q12, Q13, Q14, Q15]), "oppositeDirection" : true, "depth" : 4 * mm});
        }
        {
            var Q0;
            Q0=makeQuery(id+"F12.opExtrude","SWEPT_EDGE",EDGE,{"disambiguationData":[OSD([sQuery(id+"F6.wireOp",EDGE,"E17.top"),sQuery(id+"F6.wireOp",EDGE,"E17.left")])]});
            var Q1;
            Q1=makeQuery(id+"F10.opExtrude","SWEPT_EDGE",EDGE,{"disambiguationData":[OSD([sQuery(id+"F6.wireOp",EDGE,"E17.top"),sQuery(id+"F6.wireOp",EDGE,"E17.left")])]});
            var Q2;
            Q2=makeQuery(id+"F9.opExtrude","SWEPT_EDGE",EDGE,{"disambiguationData":[OSD([sQuery(id+"F6.wireOp",EDGE,"E17.top"),sQuery(id+"F6.wireOp",EDGE,"E17.left")])]});
            var Q3;
            Q3=makeQuery(id+"F7.opExtrude","SWEPT_EDGE",EDGE,{"disambiguationData":[OSD([sQuery(id+"F6.wireOp",EDGE,"E17.top"),sQuery(id+"F6.wireOp",EDGE,"E17.left")])]});
            var Q4;
            Q4=makeQuery(id+"F7.opExtrude","SWEPT_EDGE",EDGE,{"disambiguationData":[OSD([sQuery(id+"F6.wireOp",EDGE,"E17.bottom"),sQuery(id+"F6.wireOp",EDGE,"E17.left")])]});
            var Q5;
            Q5=makeQuery(id+"F9.opExtrude","SWEPT_EDGE",EDGE,{"disambiguationData":[OSD([sQuery(id+"F6.wireOp",EDGE,"E17.bottom"),sQuery(id+"F6.wireOp",EDGE,"E17.left")])]});
            var Q6;
            Q6=makeQuery(id+"F10.opExtrude","SWEPT_EDGE",EDGE,{"disambiguationData":[OSD([sQuery(id+"F6.wireOp",EDGE,"E17.bottom"),sQuery(id+"F6.wireOp",EDGE,"E17.left")])]});
            var Q7;
            Q7=makeQuery(id+"F12.opExtrude","SWEPT_EDGE",EDGE,{"disambiguationData":[OSD([sQuery(id+"F6.wireOp",EDGE,"E17.bottom"),sQuery(id+"F6.wireOp",EDGE,"E17.left")])]});
            var Q8;
            Q8=makeQuery(id+"F7.opExtrude","SWEPT_EDGE",EDGE,{"disambiguationData":[OSD([sQuery(id+"F6.wireOp",EDGE,"E17.bottom"),sQuery(id+"F6.wireOp",EDGE,"E17.right")])]});
            var Q9;
            Q9=makeQuery(id+"F9.opExtrude","SWEPT_EDGE",EDGE,{"disambiguationData":[OSD([sQuery(id+"F6.wireOp",EDGE,"E17.bottom"),sQuery(id+"F6.wireOp",EDGE,"E17.right")])]});
            var Q10;
            Q10=makeQuery(id+"F10.opExtrude","SWEPT_EDGE",EDGE,{"disambiguationData":[OSD([sQuery(id+"F6.wireOp",EDGE,"E17.bottom"),sQuery(id+"F6.wireOp",EDGE,"E17.right")])]});
            var Q11;
            Q11=makeQuery(id+"F12.opExtrude","SWEPT_EDGE",EDGE,{"disambiguationData":[OSD([sQuery(id+"F6.wireOp",EDGE,"E17.bottom"),sQuery(id+"F6.wireOp",EDGE,"E17.right")])]});
            var Q12;
            Q12=makeQuery(id+"F7.opExtrude","SWEPT_EDGE",EDGE,{"disambiguationData":[OSD([sQuery(id+"F6.wireOp",EDGE,"E17.top"),sQuery(id+"F6.wireOp",EDGE,"E17.right")])]});
            var Q13;
            Q13=makeQuery(id+"F9.opExtrude","SWEPT_EDGE",EDGE,{"disambiguationData":[OSD([sQuery(id+"F6.wireOp",EDGE,"E17.top"),sQuery(id+"F6.wireOp",EDGE,"E17.right")])]});
            var Q14;
            Q14=makeQuery(id+"F10.opExtrude","SWEPT_EDGE",EDGE,{"disambiguationData":[OSD([sQuery(id+"F6.wireOp",EDGE,"E17.top"),sQuery(id+"F6.wireOp",EDGE,"E17.right")])]});
            var Q15;
            Q15=makeQuery(id+"F12.opExtrude","SWEPT_EDGE",EDGE,{"disambiguationData":[OSD([sQuery(id+"F6.wireOp",EDGE,"E17.top"),sQuery(id+"F6.wireOp",EDGE,"E17.right")])]});
            var Q16;
            Q16=makeQuery(id+"F20.opExtrude","SWEPT_EDGE",EDGE,{"disambiguationData":[OSD([sQuery(id+"F6.wireOp",EDGE,"E17.bottom"),sQuery(id+"F6.wireOp",EDGE,"E17.right")])]});
            var Q17;
            Q17=makeQuery(id+"F20.opExtrude","SWEPT_EDGE",EDGE,{"disambiguationData":[OSD([sQuery(id+"F6.wireOp",EDGE,"E17.top"),sQuery(id+"F6.wireOp",EDGE,"E17.right")])]});
            var Q18;
            Q18=makeQuery(id+"F20.opExtrude","SWEPT_EDGE",EDGE,{"disambiguationData":[OSD([sQuery(id+"F6.wireOp",EDGE,"E17.bottom"),sQuery(id+"F6.wireOp",EDGE,"E17.left")])]});
            var Q19;
            Q19=makeQuery(id+"F20.opExtrude","SWEPT_EDGE",EDGE,{"disambiguationData":[OSD([sQuery(id+"F6.wireOp",EDGE,"E17.top"),sQuery(id+"F6.wireOp",EDGE,"E17.left")])]});
            fillet(context, id + "F21", {"entities" : qUnion([Q0, Q1, Q2, Q3, Q4, Q5, Q6, Q7, Q8, Q9, Q10, Q11, Q12, Q13, Q14, Q15, Q16, Q17, Q18, Q19]), "radius" : 1.9 * mm, "tangentPropagation" : true, "allowEdgeOverflow" : false});
        }
        {
            var Q0;
            Q0=makeQuery(id+"F20.opExtrude","CAP_FACE",FACE,{"disambiguationData":[OSD([sQuery(id+"F6.wireOp",EDGE,"4588470f-8c88-46ac-a9e8-f2cc96a3f2d9.1"),sQuery(id+"F6.wireOp",EDGE,"4588470f-8c88-46ac-a9e8-f2cc96a3f2d9.2"),sQuery(id+"F6.wireOp",EDGE,"4588470f-8c88-46ac-a9e8-f2cc96a3f2d9.5"),sQuery(id+"F6.wireOp",EDGE,"4588470f-8c88-46ac-a9e8-f2cc96a3f2d9.7"),sQuery(id+"F6.wireOp",EDGE,"E8"),sQuery(id+"F6.wireOp",EDGE,"E9"),sQuery(id+"F6.wireOp",EDGE,"E10"),sQuery(id+"F6.wireOp",EDGE,"E11"),sQuery(id+"F6.wireOp",EDGE,"E12"),sQuery(id+"F6.wireOp",EDGE,"E13"),sQuery(id+"F6.wireOp",EDGE,"E14"),sQuery(id+"F6.wireOp",EDGE,"E15"),sQuery(id+"F6.wireOp",EDGE,"E16.bottom"),sQuery(id+"F6.wireOp",EDGE,"E16.top"),sQuery(id+"F6.wireOp",EDGE,"E16.left"),sQuery(id+"F6.wireOp",EDGE,"E16.right")])],"isStart":false});
            var sketch = newSketch(context, id + "F22", { "sketchPlane" : qUnion([Q0])});
            skCircle(sketch, "E27", {"center": v(27.7, -23.8) * mm, "radius": 1.88 * mm});
            skCircle(sketch, "E28", {"center": v(27.7, 22.78) * mm, "radius": 1.88 * mm});
            skCircle(sketch, "E29", {"center": v(-27.72, 22.78) * mm, "radius": 1.88 * mm});
            skCircle(sketch, "E30", {"center": v(-27.72, -23.8) * mm, "radius": 1.88 * mm});
            skSolve(sketch);
        }
        {
            var Q0;
            Q0=makeQuery(id+"F22.imprint","IMPRINT",FACE,{"disambiguationData":[TD([[makeQuery(id+"F22.imprint","IMPRINT",EDGE,{"derivedFrom":sQuery(id+"F22.wireOp",EDGE,"E28")}),1.0]])]});
            var Q1;
            Q1=makeQuery(id+"F22.imprint","IMPRINT",FACE,{"disambiguationData":[TD([[makeQuery(id+"F22.imprint","IMPRINT",EDGE,{"derivedFrom":sQuery(id+"F22.wireOp",EDGE,"E29")}),1.0]])]});
            var Q2;
            Q2=makeQuery(id+"F22.imprint","IMPRINT",FACE,{"disambiguationData":[TD([[makeQuery(id+"F22.imprint","IMPRINT",EDGE,{"derivedFrom":sQuery(id+"F22.wireOp",EDGE,"E30")}),1.0]])]});
            var Q3;
            Q3=makeQuery(id+"F22.imprint","IMPRINT",FACE,{"disambiguationData":[TD([[makeQuery(id+"F22.imprint","IMPRINT",EDGE,{"derivedFrom":sQuery(id+"F22.wireOp",EDGE,"E27")}),1.0]])]});
            extrude(context, id + "F23", {"entities" : qUnion([Q0, Q1, Q2, Q3]), "operationType" : NewBodyOperationType.ADD, "depth" : 50 * mm});
        }
        {
            var Q0;
            Q0=makeQuery(id+"F19.imprint","IMPRINT",FACE,{"disambiguationData":[TD([[makeQuery(id+"F19.imprint","IMPRINT",EDGE,{"derivedFrom":makeQuery(id+"F18.opExtrude","CAP_EDGE",EDGE,{"disambiguationData":[OSD([sQuery(id+"F16.wireOp",EDGE,"E24")])],"isStart":false})}),-1.0]])]});
            var Q1;
            Q1=makeQuery(id+"F19.imprint","IMPRINT",FACE,{"disambiguationData":[TD([[makeQuery(id+"F19.imprint","IMPRINT",EDGE,{"derivedFrom":sQuery(id+"F19.wireOp",EDGE,"E26")}),1.0]])]});
            extrude(context, id + "F24", {"entities" : qUnion([Q0, Q1]), "operationType" : NewBodyOperationType.ADD, "depth" : 6 * mm});
        }
        {
            var Q0;
            Q0=makeQuery(id+"F24.opExtrude","CAP_FACE",FACE,{"disambiguationData":[OSD([sQuery(id+"F19.wireOp",EDGE,"E26")])],"isStart":false});
            var sketch = newSketch(context, id + "F25", { "sketchPlane" : qUnion([Q0])});
            skCircle(sketch, "E31", {"center": v(8, 8) * mm, "radius": 11.25 * mm});
            skLineSegment(sketch, "E32", {"start": v(23.27, 19.27) * mm, "end": v(-6.73, 19.23) * mm});
            skLineSegment(sketch, "E33", {"start": v(23.24, 35.27) * mm, "end": v(-6.76, 35.23) * mm});
            skLineSegment(sketch, "E34", {"start": v(23.24, 35.27) * mm, "end": v(23.27, 19.27) * mm});
            skLineSegment(sketch, "E35", {"start": v(-6.76, 35.23) * mm, "end": v(-6.73, 19.23) * mm});
            skLineSegment(sketch, "E36", {"start": v(23.27, 19.27) * mm, "end": v(18.75, 4.67) * mm});
            skLineSegment(sketch, "E37", {"start": v(-6.73, 19.23) * mm, "end": v(-2.85, 5.03) * mm});
            skSolve(sketch);
        }
        {
            var Q0;
            Q0=makeQuery(id+"F25.imprint","IMPRINT",FACE,{"disambiguationData":[TD([[makeQuery(id+"F25.imprint","IMPRINT",EDGE,{"derivedFrom":sQuery(id+"F25.wireOp",EDGE,"E31")}),1.0]])]});
            var Q1;
            Q1=makeQuery(id+"F25.imprint","IMPRINT",FACE,{"disambiguationData":[TD([[makeQuery(id+"F25.imprint","IMPRINT",EDGE,{"derivedFrom":makeQuery(id+"F24.opExtrude","CAP_EDGE",EDGE,{"disambiguationData":[OSD([sQuery(id+"F19.wireOp",EDGE,"E26")])],"isStart":false})}),1.0]])]});
            extrude(context, id + "F26", {"entities" : qUnion([Q0, Q1]), "operationType" : NewBodyOperationType.ADD, "depth" : 28 * mm});
        }
        {
            var Q0;
            {var subQ4=sQuery(id+"F25.wireOp",EDGE,"E32");Q0=makeQuery(id+"F25.imprint","IMPRINT",FACE,{"disambiguationData":[TD([[makeQuery(id+"F25.imprint","IMPRINT",EDGE,{"derivedFrom":subQ4}),1.0]])]});}
            var Q1;
            Q1=makeQuery(id+"F25.imprint","IMPRINT",FACE,{"disambiguationData":[TD([[makeQuery(id+"F25.imprint","IMPRINT",EDGE,{"derivedFrom":sQuery(id+"F25.wireOp",EDGE,"E33")}),1.0]])]});
            extrude(context, id + "F27", {"entities" : qUnion([Q0, Q1]), "operationType" : NewBodyOperationType.ADD, "depth" : 25 * mm});
        }
        {
            var Q0;
            Q0=makeQuery(id+"F20.opExtrude","CAP_FACE",FACE,{"disambiguationData":[OSD([sQuery(id+"F6.wireOp",EDGE,"4588470f-8c88-46ac-a9e8-f2cc96a3f2d9.1"),sQuery(id+"F6.wireOp",EDGE,"4588470f-8c88-46ac-a9e8-f2cc96a3f2d9.2"),sQuery(id+"F6.wireOp",EDGE,"4588470f-8c88-46ac-a9e8-f2cc96a3f2d9.5"),sQuery(id+"F6.wireOp",EDGE,"4588470f-8c88-46ac-a9e8-f2cc96a3f2d9.7"),sQuery(id+"F6.wireOp",EDGE,"E8"),sQuery(id+"F6.wireOp",EDGE,"E9"),sQuery(id+"F6.wireOp",EDGE,"E10"),sQuery(id+"F6.wireOp",EDGE,"E11"),sQuery(id+"F6.wireOp",EDGE,"E12"),sQuery(id+"F6.wireOp",EDGE,"E13"),sQuery(id+"F6.wireOp",EDGE,"E14"),sQuery(id+"F6.wireOp",EDGE,"E15"),sQuery(id+"F6.wireOp",EDGE,"E16.bottom"),sQuery(id+"F6.wireOp",EDGE,"E16.top"),sQuery(id+"F6.wireOp",EDGE,"E16.left"),sQuery(id+"F6.wireOp",EDGE,"E16.right")])],"isStart":false});
            var sketch = newSketch(context, id + "F28", { "sketchPlane" : qUnion([Q0])});
            skLineSegment(sketch, "E38.bottom", {"start": v(-20.1, 22.23) * mm, "end": v(19.9, 22.23) * mm});
            skLineSegment(sketch, "E38.top", {"start": v(-20.1, -21.77) * mm, "end": v(19.9, -21.77) * mm});
            skLineSegment(sketch, "E38.left", {"start": v(-20.1, 22.23) * mm, "end": v(-20.1, -21.77) * mm});
            skLineSegment(sketch, "E38.right", {"start": v(19.9, 22.23) * mm, "end": v(19.9, -21.77) * mm});
            skSolve(sketch);
        }
        {
            var Q0;
            Q0=makeQuery(id+"F28.imprint","IMPRINT",FACE,{"disambiguationData":[TD([[makeQuery(id+"F28.imprint","IMPRINT",EDGE,{"derivedFrom":sQuery(id+"F28.wireOp",EDGE,"E38.bottom")}),-1.0]])]});
            var Q1;
            Q1=makeQuery(id+"F28.imprint","IMPRINT",FACE,{"disambiguationData":[TD([[makeQuery(id+"F28.imprint","IMPRINT",EDGE,{"derivedFrom":makeQuery(id+"F20.opExtrude","CAP_EDGE",EDGE,{"disambiguationData":[OSD([sQuery(id+"F6.wireOp",EDGE,"4588470f-8c88-46ac-a9e8-f2cc96a3f2d9.1")])],"isStart":false})}),1.0]])]});
            var Q2;
            {var subQ6=sQuery(id+"F6.wireOp",EDGE,"E8");Q2=makeQuery(id+"F28.imprint","IMPRINT",FACE,{"disambiguationData":[TD([[makeQuery(id+"F28.imprint","IMPRINT",EDGE,{"derivedFrom":makeQuery(id+"F20.opExtrude","CAP_EDGE",EDGE,{"disambiguationData":[OSD([subQ6])],"isStart":false})}),1.0]])]});}
            var Q3;
            Q3=makeQuery(id+"F28.imprint","IMPRINT",FACE,{"disambiguationData":[TD([[makeQuery(id+"F28.imprint","IMPRINT",EDGE,{"derivedFrom":makeQuery(id+"F20.opExtrude","CAP_EDGE",EDGE,{"disambiguationData":[OSD([sQuery(id+"F6.wireOp",EDGE,"E12")])],"isStart":false})}),1.0]])]});
            extrude(context, id + "F29", {"entities" : qUnion([Q0, Q1, Q2, Q3]), "depth" : 6 * mm});
        }
    });
